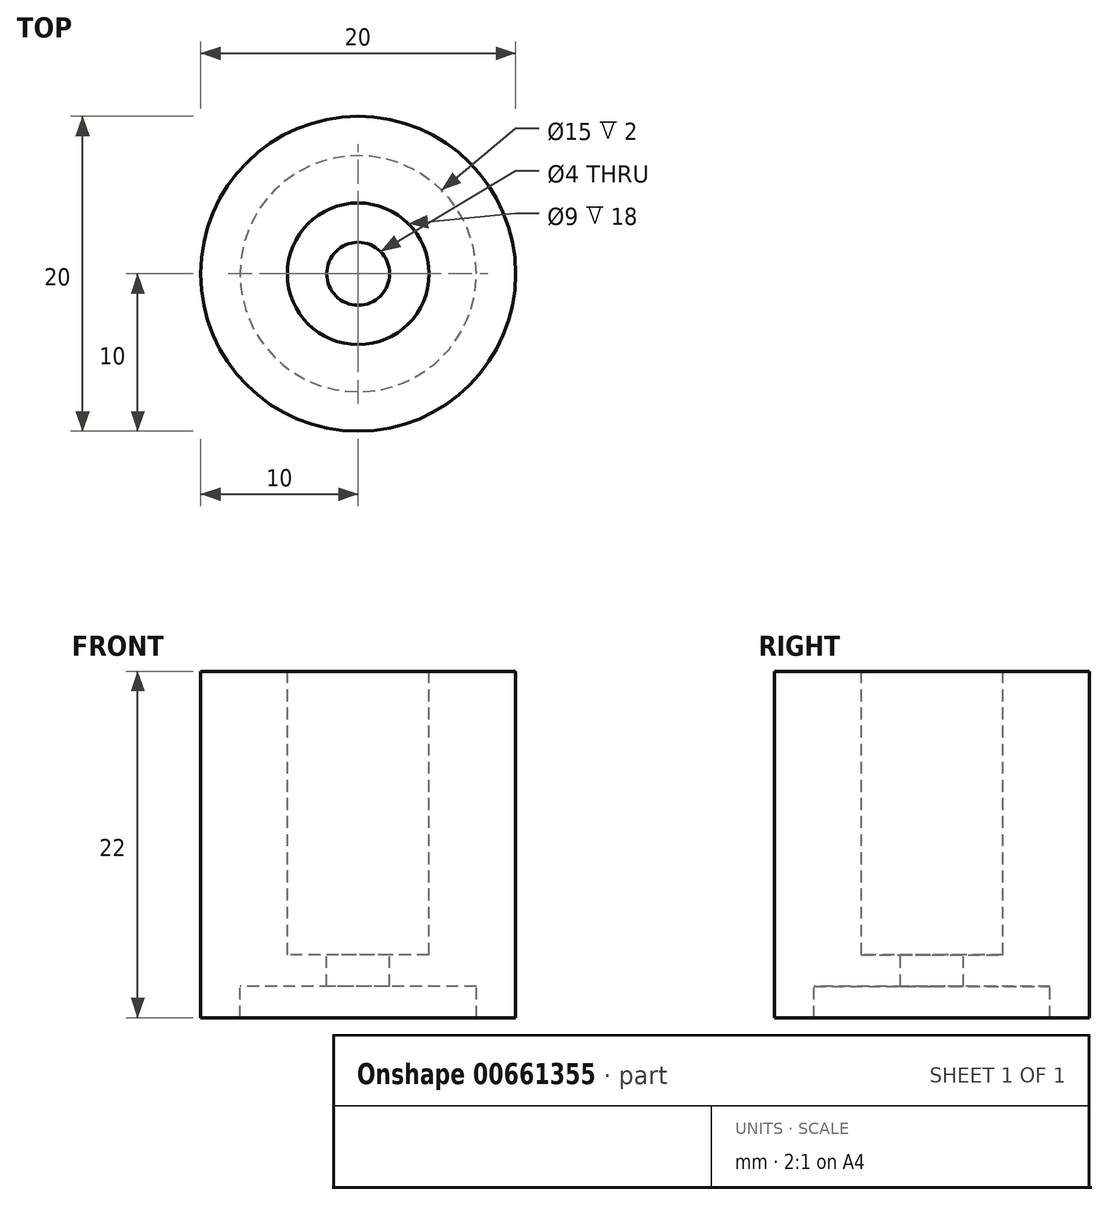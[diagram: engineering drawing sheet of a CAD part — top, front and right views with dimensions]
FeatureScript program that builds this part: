
annotation { "Feature Type Name" : "Feature", "Feature Type Description" : "" }
export const myFeature = defineFeature(function(context is Context, id is Id, definition is map)
    precondition{}
    {
        {
            var Q0;
            Q0=qCreatedBy(makeId("Front.planeOp"),FACE);
            var sketch = newSketch(context, id + "F0", { "sketchPlane" : qUnion([Q0])});
            skLineSegment(sketch, "E0", {"start": v(0, 0) * mm, "end": v(-10, 0) * mm, "construction": true});
            skLineSegment(sketch, "E1", {"start": v(-10, 0) * mm, "end": v(-10, 22) * mm});
            skLineSegment(sketch, "E2", {"start": v(-10, 0) * mm, "end": v(-7.5, 0) * mm});
            skLineSegment(sketch, "E3", {"start": v(-10, 22) * mm, "end": v(-4.5, 22) * mm});
            skLineSegment(sketch, "E4", {"start": v(-4.5, 22) * mm, "end": v(-4.5, 4) * mm});
            skLineSegment(sketch, "E5", {"start": v(-4.5, 4) * mm, "end": v(-2, 4) * mm});
            skLineSegment(sketch, "E6", {"start": v(-2, 4) * mm, "end": v(-2, 2) * mm});
            skLineSegment(sketch, "E7", {"start": v(-7.5, 0) * mm, "end": v(-7.5, 2) * mm});
            skLineSegment(sketch, "E8", {"start": v(-7.5, 2) * mm, "end": v(-2, 2) * mm});
            skLineSegment(sketch, "E9", {"start": v(0, 22) * mm, "end": v(0, 0) * mm, "construction": true});
            skSolve(sketch);
        }
        {
            var Q0;
            Q0 = qSketchRegion(id + "F0", true);
            var Q1;
            Q1=sQuery(id+"F0.wireOp",EDGE,"E9");
            revolve(context, id + "F1", {"entities" : qUnion([Q0]), "axis" : qUnion([Q1]), "revolveType" : RevolveType.FULL});
        }
    });
